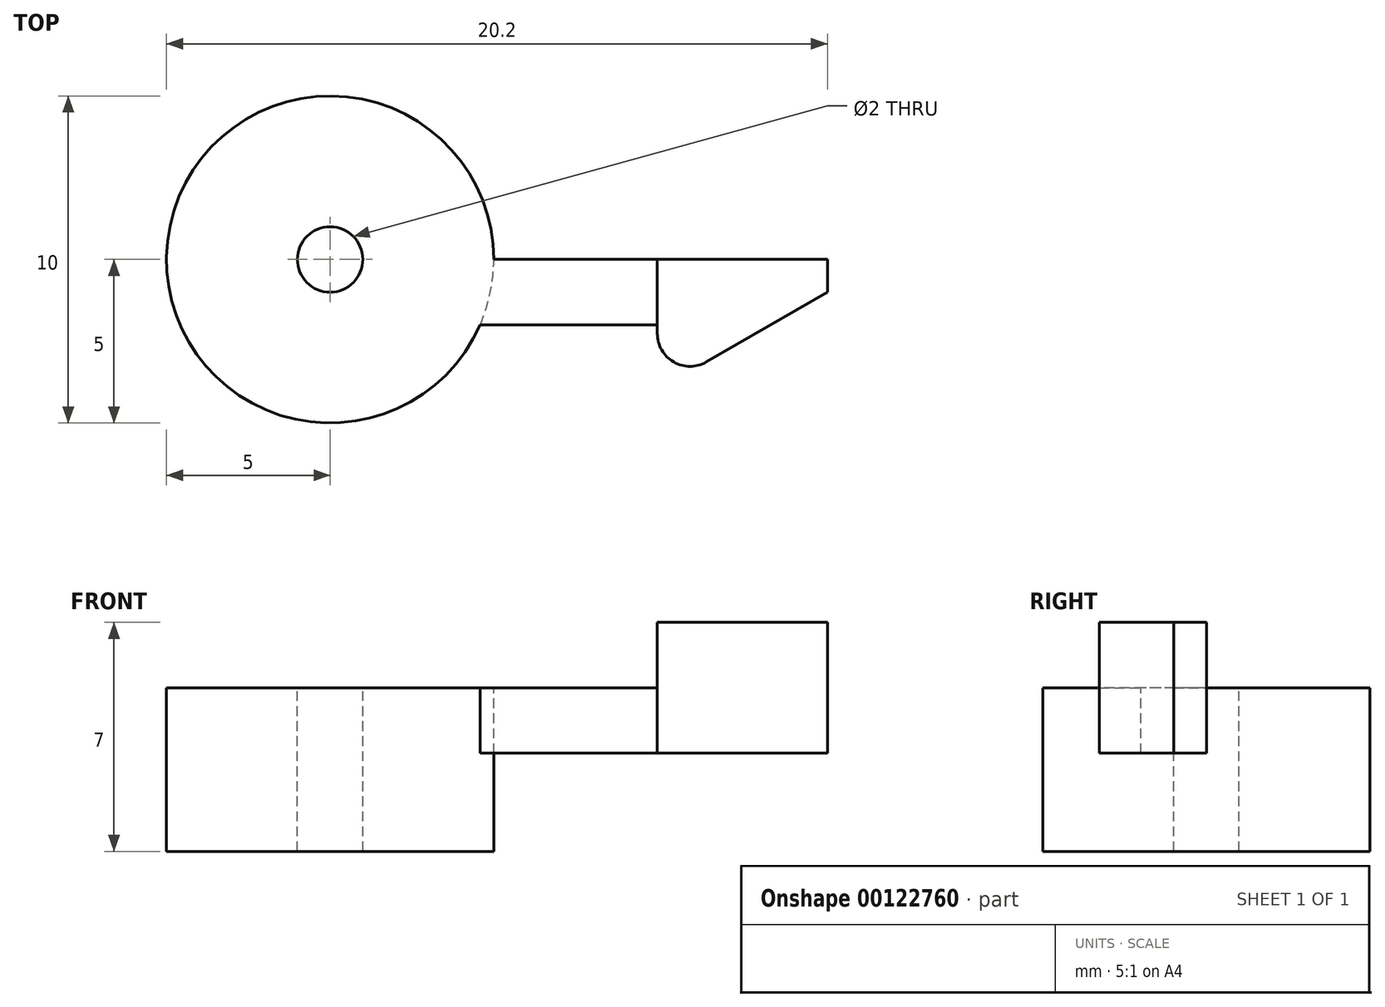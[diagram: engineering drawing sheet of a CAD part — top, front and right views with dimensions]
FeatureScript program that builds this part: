
annotation { "Feature Type Name" : "Feature", "Feature Type Description" : "" }
export const myFeature = defineFeature(function(context is Context, id is Id, definition is map)
    precondition{}
    {
        {
            var Q0;
            Q0=qCreatedBy(makeId("Top.planeOp"),FACE);
            var sketch = newSketch(context, id + "F0", { "sketchPlane" : qUnion([Q0])});
            skCircle(sketch, "E0", {"center": v(0, 0) * mm, "radius": 5 * mm});
            skLineSegment(sketch, "E1", {"start": v(5, 0) * mm, "end": v(10, 0) * mm});
            skLineSegment(sketch, "E2", {"start": v(15.2, 0) * mm, "end": v(10, 0) * mm});
            skLineSegment(sketch, "E3.MirrorCS", {"start": v(10, -2) * mm, "end": v(4.58, -2) * mm});
            skLineSegment(sketch, "E4.MirrorCS", {"start": v(10, 0) * mm, "end": v(10, -2) * mm});
            skLineSegment(sketch, "E5.MirrorCS", {"start": v(10, -2) * mm, "end": v(10, -4) * mm});
            skLineSegment(sketch, "E6.MirrorCS", {"start": v(10, -4) * mm, "end": v(15.2, -1) * mm});
            skLineSegment(sketch, "E7.MirrorCS", {"start": v(15.2, -1) * mm, "end": v(15.2, 0) * mm});
            skLineSegment(sketch, "E8", {"start": v(5, 0) * mm, "end": v(15.2, 0) * mm});
            skSolve(sketch);
        }
        {
            var Q0;
            {var subQ0=sQuery(id+"F0.wireOp",EDGE,"E0");var subQ1=makeQuery(id+"F0.imprint","INTERSECT",VERTEX,{"derivedFrom":[subQ0,sQuery(id+"F0.wireOp",EDGE,"E3.MirrorCS")]});Q0=makeQuery(id+"F0.imprint","IMPRINT",FACE,{"disambiguationData":[TD([[makeQuery(id+"F0.imprint","IMPRINT",EDGE,{"disambiguationData":[TD([[subQ1,1.0]])],"derivedFrom":subQ0}),1.0]])]});}
            extrude(context, id + "F1", {"entities" : qUnion([Q0]), "oppositeDirection" : true, "depth" : 5 * mm});
        }
        {
            var Q0;
            {var subQ4=sQuery(id+"F0.wireOp",EDGE,"E4.MirrorCS");Q0=makeQuery(id+"F0.imprint","IMPRINT",FACE,{"disambiguationData":[TD([[makeQuery(id+"F0.imprint","IMPRINT",EDGE,{"derivedFrom":subQ4}),-1.0]])]});}
            extrude(context, id + "F2", {"entities" : qUnion([Q0]), "operationType" : NewBodyOperationType.ADD, "oppositeDirection" : true, "depth" : 2 * mm});
        }
        {
            var Q0;
            {var subQ1=sQuery(id+"F0.wireOp",EDGE,"E4.MirrorCS");Q0=makeQuery(id+"F0.imprint","IMPRINT",FACE,{"disambiguationData":[TD([[makeQuery(id+"F0.imprint","IMPRINT",EDGE,{"derivedFrom":subQ1}),1.0]])]});}
            extrude(context, id + "F3", {"entities" : qUnion([Q0]), "operationType" : NewBodyOperationType.ADD, "endBound" : BoundingType.SYMMETRIC, "depth" : 4 * mm});
        }
        {
            var Q0;
            Q0=makeQuery(id+"F3.opExtrude","SWEPT_EDGE",EDGE,{"disambiguationData":[OSD([sQuery(id+"F0.wireOp",EDGE,"E5.MirrorCS"),sQuery(id+"F0.wireOp",EDGE,"E6.MirrorCS")])]});
            fillet(context, id + "F4", {"entities" : qUnion([Q0]), "radius" : 1 * mm, "tangentPropagation" : true, "allowEdgeOverflow" : false});
        }
        {
            var Q0;
            Q0=sQuery(id+"F0.wireOp",VERTEX,"E0.center");
            var Q1;
            Q1=makeQuery(id+"F1.opExtrude","SWEPT_BODY",BODY,{"disambiguationData":[OSD([sQuery(id+"F0.wireOp",EDGE,"E0")])]});
            hole(context, id + "F5", {"style" : HoleStyle.SIMPLE, "endStyle" : HoleEndStyle.THROUGH, "holeDiameter" : 2 * mm, "locations" : qUnion([Q0]), "scope" : qUnion([Q1]), "isTappedThrough" : true});
        }
    });
